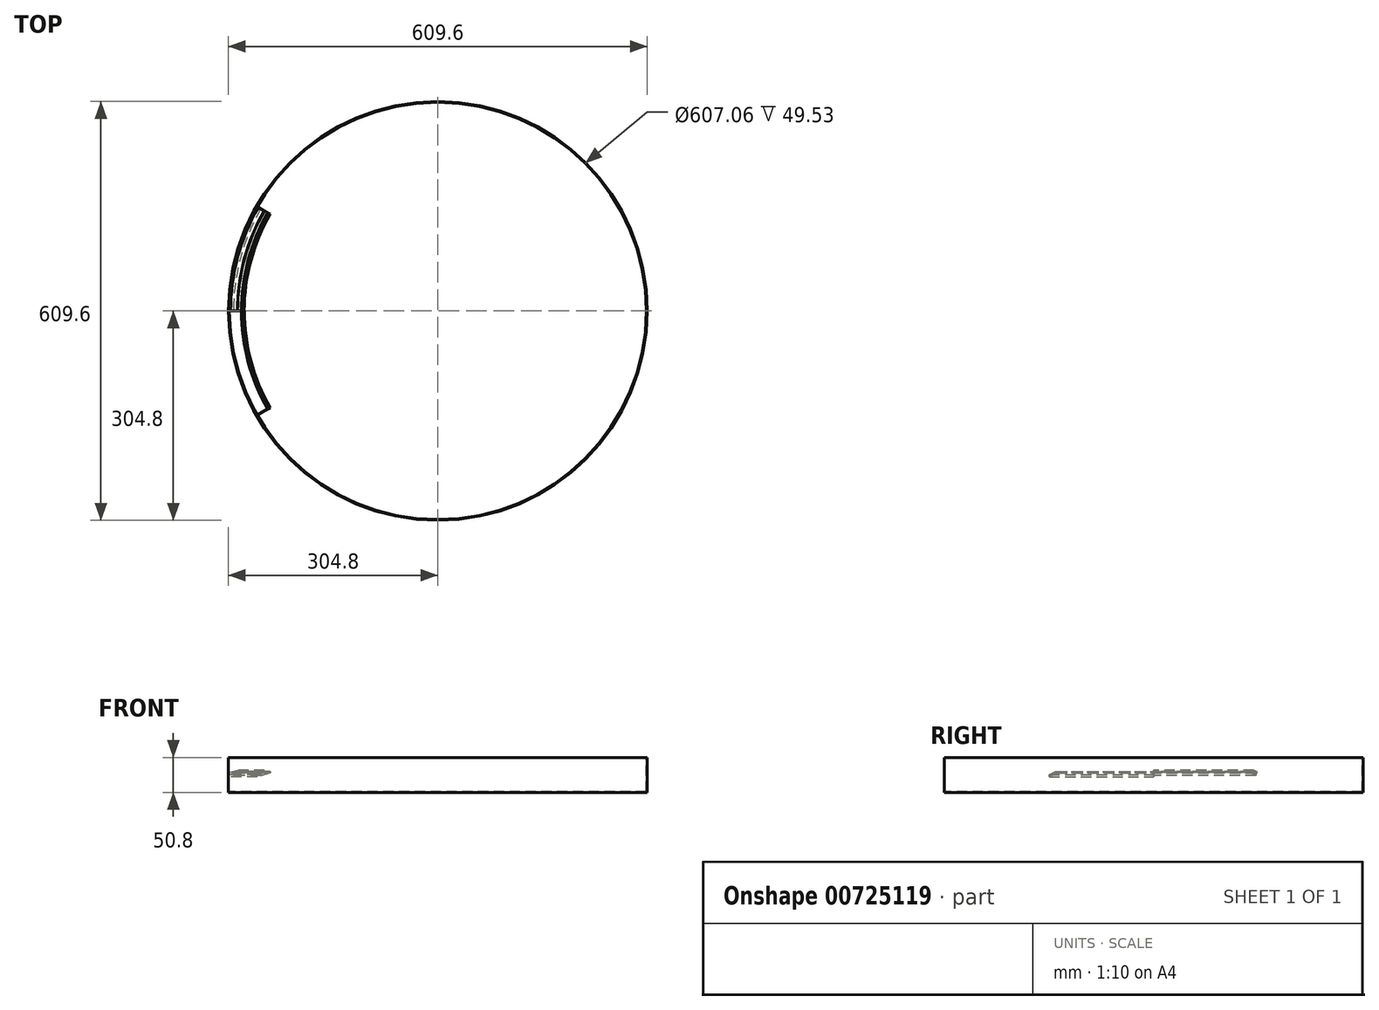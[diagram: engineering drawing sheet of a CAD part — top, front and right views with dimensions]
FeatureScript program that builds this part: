
annotation { "Feature Type Name" : "Feature", "Feature Type Description" : "" }
export const myFeature = defineFeature(function(context is Context, id is Id, definition is map)
    precondition{}
    {
        {
            var Q0;
            Q0=qCreatedBy(makeId("Front.planeOp"),FACE);
            var sketch = newSketch(context, id + "F0", { "sketchPlane" : qUnion([Q0])});
            skLineSegment(sketch, "E0.left", {"start": v(-304.8, -3.12) * mm, "end": v(-304.8, -28.52) * mm});
            skPoint(sketch, "E1.orphan", {"position": v(-304.8, 0) * mm});
            skLineSegment(sketch, "E2", {"start": v(-304.8, -3.12) * mm, "end": v(-304.8, 22.28) * mm});
            skLineSegment(sketch, "E3", {"start": v(-304.8, 22.28) * mm, "end": v(-303.53, 22.28) * mm});
            skLineSegment(sketch, "E4", {"start": v(-303.53, 22.28) * mm, "end": v(-303.53, -2.78) * mm});
            skLineSegment(sketch, "E5", {"start": v(-304.8, -28.52) * mm, "end": v(0, -28.52) * mm});
            skLineSegment(sketch, "E6", {"start": v(-303.53, -27.25) * mm, "end": v(-303.53, -4.1) * mm});
            skLineSegment(sketch, "E7", {"start": v(-303.53, -27.25) * mm, "end": v(0, -27.25) * mm});
            skLineSegment(sketch, "E8", {"start": v(0, -28.52) * mm, "end": v(0, -27.25) * mm});
            skLineSegment(sketch, "E9", {"start": v(-303.53, -2.78) * mm, "end": v(-303.53, -4.1) * mm});
            skLineSegment(sketch, "E10", {"start": v(-295.28, -0.57) * mm, "end": v(-297.44, -1.15) * mm});
            skLineSegment(sketch, "E11", {"start": v(-295.28, -0.57) * mm, "end": v(-285.75, 1.99) * mm});
            skLineSegment(sketch, "E12", {"start": v(-297.44, -3.93) * mm, "end": v(-283.93, -0.32) * mm});
            skLineSegment(sketch, "E13", {"start": v(-285.36, 0.51) * mm, "end": v(-285.75, 1.99) * mm});
            skLineSegment(sketch, "E14", {"start": v(-285.36, 0.51) * mm, "end": v(-281.7, 1.58) * mm});
            skLineSegment(sketch, "E15", {"start": v(-297.44, -1.15) * mm, "end": v(-297.44, -3.93) * mm});
            skLineSegment(sketch, "E16", {"start": v(-291.26, 2.22) * mm, "end": v(-301.17, -0.44) * mm});
            skLineSegment(sketch, "E17", {"start": v(-301.17, -0.44) * mm, "end": v(-301.5, 0.8) * mm});
            skLineSegment(sketch, "E18", {"start": v(-301.5, 0.8) * mm, "end": v(-291.6, 3.45) * mm});
            skLineSegment(sketch, "E19", {"start": v(-291.26, 2.22) * mm, "end": v(-291.6, 3.45) * mm});
            skLineSegment(sketch, "E20", {"start": v(-281.7, 1.58) * mm, "end": v(-281.7, 0.28) * mm});
            skLineSegment(sketch, "E21", {"start": v(-283.93, -0.32) * mm, "end": v(-281.7, 0.28) * mm});
            skSolve(sketch);
        }
        {
            var Q0;
            Q0=qCreatedBy(makeId("Front.planeOp"),FACE);
            var sketch = newSketch(context, id + "F1", { "sketchPlane" : qUnion([Q0])});
            skLineSegment(sketch, "E22", {"start": v(0, 40.5) * mm, "end": v(0, -62.38) * mm});
            skSolve(sketch);
        }
        {
            var Q0;
            Q0=makeQuery(id+"F0.imprint","IMPRINT",FACE,{"disambiguationData":[TD([[makeQuery(id+"F0.imprint","IMPRINT",EDGE,{"derivedFrom":sQuery(id+"F0.wireOp",EDGE,"E0.left")}),1.0]])]});
            var Q1;
            Q1=sQuery(id+"F1.wireOp",EDGE,"E22");
            revolve(context, id + "F2", {"surfaceOperationType" : NewSurfaceOperationType.NEW, "entities" : qUnion([Q0]), "axis" : qUnion([Q1]), "revolveType" : RevolveType.FULL});
        }
        {
            var Q0;
            Q0=qCreatedBy(makeId("Front.planeOp"),FACE);
            var sketch = newSketch(context, id + "F3", { "sketchPlane" : qUnion([Q0])});
            skLineSegment(sketch, "E23", {"start": v(-303.53, -2.77) * mm, "end": v(-285.74, 2) * mm});
            skLineSegment(sketch, "E24", {"start": v(-281.52, -0.15) * mm, "end": v(-303.5, -6.05) * mm});
            skLineSegment(sketch, "E25", {"start": v(-303.5, -6.05) * mm, "end": v(-303.53, -2.77) * mm});
            skLineSegment(sketch, "E26", {"start": v(-285.74, 2) * mm, "end": v(-285.35, 0.55) * mm});
            skLineSegment(sketch, "E27", {"start": v(-285.35, 0.55) * mm, "end": v(-281.52, 1.58) * mm});
            skLineSegment(sketch, "E28", {"start": v(-281.52, 1.58) * mm, "end": v(-281.52, -0.15) * mm});
            skSolve(sketch);
        }
        {
            var Q0;
            Q0=makeQuery(id+"F0.imprint","IMPRINT",FACE,{"disambiguationData":[TD([[makeQuery(id+"F0.imprint","IMPRINT",EDGE,{"derivedFrom":sQuery(id+"F0.wireOp",EDGE,"E10")}),1.0]])]});
            var Q1;
            Q1=makeQuery(id+"F0.imprint","IMPRINT",FACE,{"disambiguationData":[TD([[makeQuery(id+"F0.imprint","IMPRINT",EDGE,{"derivedFrom":sQuery(id+"F0.wireOp",EDGE,"E16")}),-1.0]])]});
            var Q2;
            Q2=sQuery(id+"F1.wireOp",EDGE,"E22");
            revolve(context, id + "F4", {"surfaceOperationType" : NewSurfaceOperationType.NEW, "entities" : qUnion([Q0, Q1]), "axis" : qUnion([Q2]), "revolveType" : RevolveType.ONE_DIRECTION, "angle" : 30 * degree});
        }
        {
            var Q0;
            {var subQ0=sQuery(id+"F3.wireOp",EDGE,"E24");Q0=makeQuery(id+"F3.imprint","IMPRINT",FACE,{"disambiguationData":[TD([[makeQuery(id+"F3.imprint","IMPRINT",EDGE,{"derivedFrom":subQ0}),-1.0]])]});}
            var Q1;
            Q1=sQuery(id+"F1.wireOp",EDGE,"E22");
            revolve(context, id + "F5", {"operationType" : NewBodyOperationType.ADD, "surfaceOperationType" : NewSurfaceOperationType.NEW, "entities" : qUnion([Q0]), "axis" : qUnion([Q1]), "revolveType" : RevolveType.ONE_DIRECTION, "oppositeDirection" : true, "angle" : 30 * degree});
        }
    });
